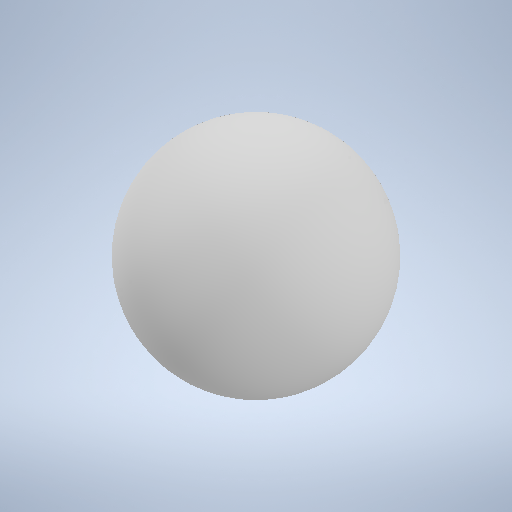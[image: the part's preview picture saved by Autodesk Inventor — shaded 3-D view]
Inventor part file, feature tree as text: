
AUTODESK INVENTOR PART (.ipt)
format: ipt  version: 2025.2 (Build 292293000, 293)  size: 254,976 bytes
history: native  units: mm
features: revolve x1, sketch x1
ambient origin geometry x8: Origin, YZ Plane, XZ Plane, XY Plane, X Axis, Y Axis, Z Axis, Center Point
bodies: Solid1 (feature_tree)
feature tree (2):
  revolve  "Revolution1"  Angle=360.0deg
  sketch  "Sketch1"  dims[d2=8.0mm d3=360.0deg d1=0.5mm d4=0.872665mm]
